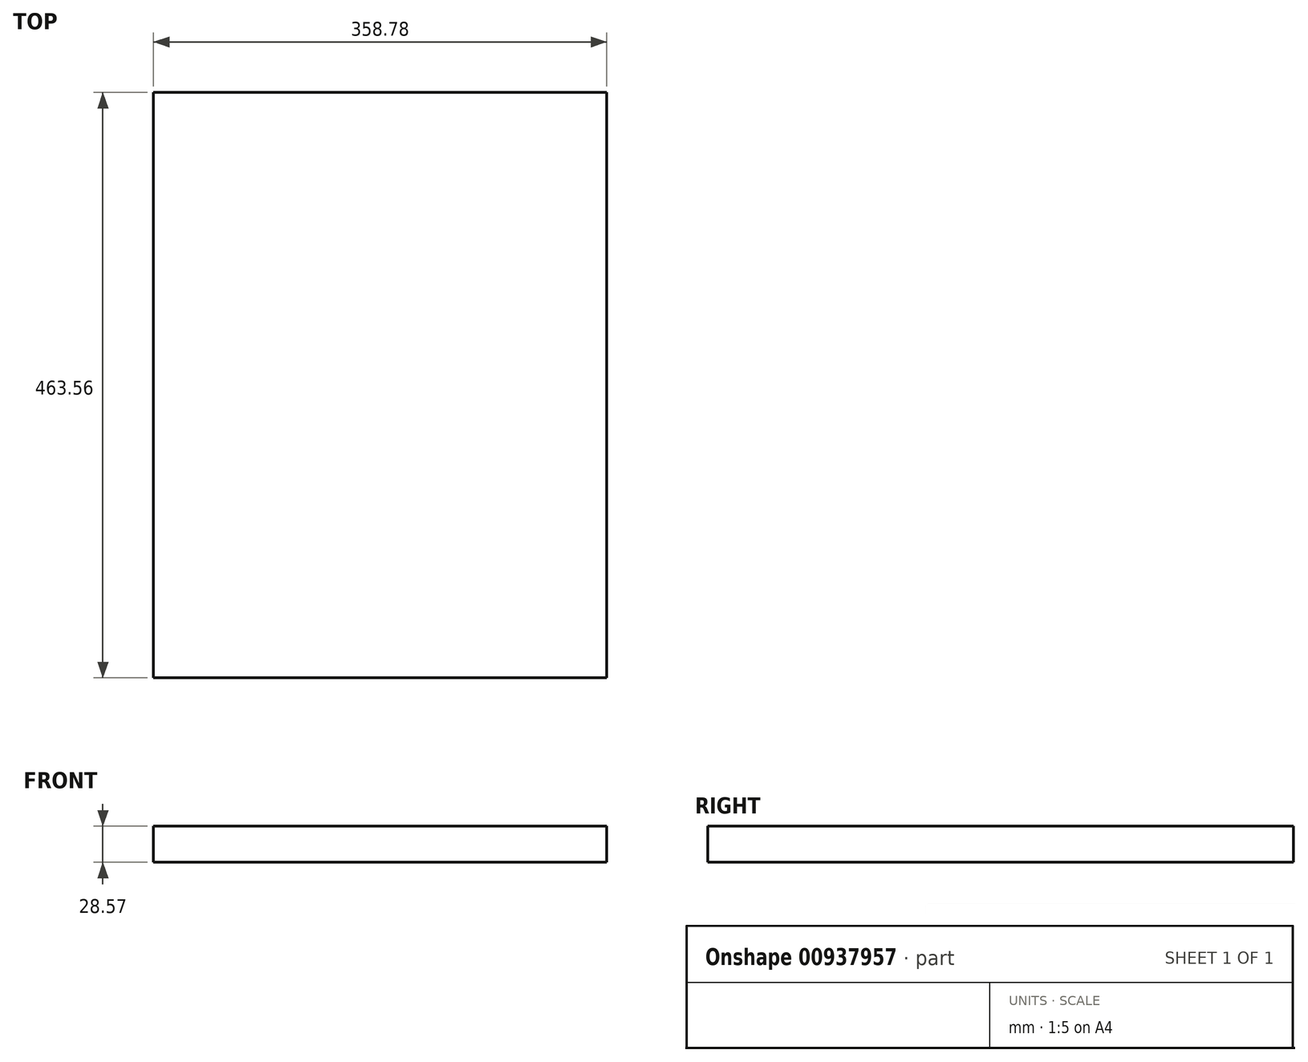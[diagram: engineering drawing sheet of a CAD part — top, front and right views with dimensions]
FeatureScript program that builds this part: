
annotation { "Feature Type Name" : "Feature", "Feature Type Description" : "" }
export const myFeature = defineFeature(function(context is Context, id is Id, definition is map)
    precondition{}
    {
        {
            var Q0;
            Q0=qCreatedBy(makeId("Top.planeOp"),FACE);
            var sketch = newSketch(context, id + "F0", { "sketchPlane" : qUnion([Q0])});
            skLineSegment(sketch, "E0.bottom", {"start": v(179.39, 231.78) * mm, "end": v(-179.39, 231.78) * mm});
            skLineSegment(sketch, "E0.top", {"start": v(179.39, -231.77) * mm, "end": v(-179.39, -231.77) * mm});
            skLineSegment(sketch, "E0.left", {"start": v(179.39, 231.78) * mm, "end": v(179.39, -231.77) * mm});
            skLineSegment(sketch, "E0.right", {"start": v(-179.39, 231.78) * mm, "end": v(-179.39, -231.77) * mm});
            skPoint(sketch, "E0.middle", {"position": v(0, 0) * mm});
            skSolve(sketch);
        }
        {
            var Q0;
            Q0=makeQuery(id+"F0.imprint","IMPRINT",FACE,{"disambiguationData":[TD([[makeQuery(id+"F0.imprint","IMPRINT",EDGE,{"derivedFrom":sQuery(id+"F0.wireOp",EDGE,"E0.bottom")}),1.0]])]});
            extrude(context, id + "F1", {"entities" : qUnion([Q0]), "depth" : 28.57 * mm, "offsetDistance" : 25.4 * mm});
        }
    });
